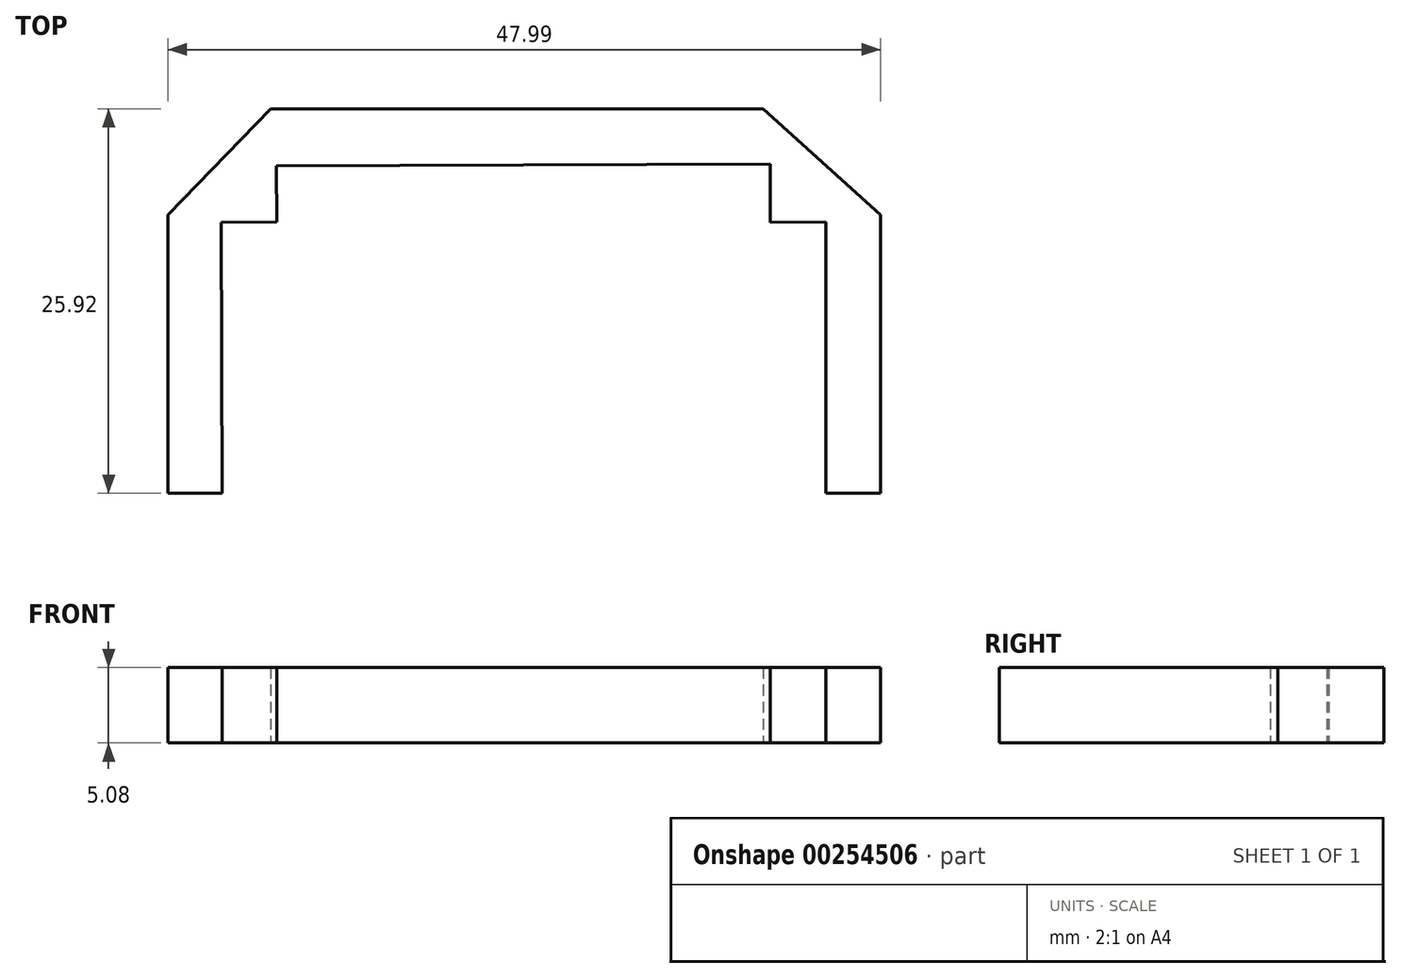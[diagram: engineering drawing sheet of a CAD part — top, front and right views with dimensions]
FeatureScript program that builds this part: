
annotation { "Feature Type Name" : "Feature", "Feature Type Description" : "" }
export const myFeature = defineFeature(function(context is Context, id is Id, definition is map)
    precondition{}
    {
        {
            var Q0;
            Q0=qCreatedBy(makeId("Top.planeOp"),FACE);
            var sketch = newSketch(context, id + "F0", { "sketchPlane" : qUnion([Q0])});
            skLineSegment(sketch, "E0", {"start": v(-33.45, 9.2) * mm, "end": v(-26.8, 16.12) * mm});
            skLineSegment(sketch, "E1", {"start": v(-26.8, 16.12) * mm, "end": v(-22.17, 16.12) * mm});
            skLineSegment(sketch, "E2", {"start": v(-22.17, 16.12) * mm, "end": v(-22.17, 19.99) * mm});
            skLineSegment(sketch, "E3", {"start": v(-22.17, 19.99) * mm, "end": v(-25.8, 19.97) * mm});
            skLineSegment(sketch, "E4", {"start": v(-25.8, 19.97) * mm, "end": v(-25.8, 38.73) * mm});
            skLineSegment(sketch, "E5", {"start": v(-25.8, 38.73) * mm, "end": v(-18.88, 45.9) * mm});
            skLineSegment(sketch, "E6", {"start": v(-18.88, 45.9) * mm, "end": v(14.3, 45.9) * mm});
            skLineSegment(sketch, "E7", {"start": v(14.3, 45.9) * mm, "end": v(22.2, 38.73) * mm});
            skLineSegment(sketch, "E8", {"start": v(22.2, 38.73) * mm, "end": v(22.2, 19.97) * mm});
            skLineSegment(sketch, "E9", {"start": v(22.2, 19.97) * mm, "end": v(18.52, 19.97) * mm});
            skLineSegment(sketch, "E10", {"start": v(18.52, 19.97) * mm, "end": v(18.52, 16.12) * mm});
            skLineSegment(sketch, "E11", {"start": v(18.52, 16.12) * mm, "end": v(22.2, 16.12) * mm});
            skLineSegment(sketch, "E12", {"start": v(22.2, 16.12) * mm, "end": v(29.83, 9.43) * mm});
            skLineSegment(sketch, "E13", {"start": v(29.83, 9.43) * mm, "end": v(29.83, -20.85) * mm});
            skLineSegment(sketch, "E14", {"start": v(29.83, -20.85) * mm, "end": v(22.14, -20.85) * mm});
            skLineSegment(sketch, "E15", {"start": v(22.14, -20.85) * mm, "end": v(22.14, -32.04) * mm});
            skLineSegment(sketch, "E16", {"start": v(22.14, -32.04) * mm, "end": v(19.03, -35.7) * mm});
            skLineSegment(sketch, "E17", {"start": v(19.03, -35.7) * mm, "end": v(3.87, -35.7) * mm});
            skLineSegment(sketch, "E18", {"start": v(3.87, -35.7) * mm, "end": v(3.87, -28.47) * mm});
            skLineSegment(sketch, "E19", {"start": v(3.87, -28.47) * mm, "end": v(-7.29, -28.47) * mm});
            skLineSegment(sketch, "E20", {"start": v(-7.29, -28.47) * mm, "end": v(-7.29, -35.7) * mm});
            skLineSegment(sketch, "E21", {"start": v(-7.29, -35.7) * mm, "end": v(-23.05, -35.7) * mm});
            skLineSegment(sketch, "E22", {"start": v(-23.05, -35.7) * mm, "end": v(-25.8, -32.44) * mm});
            skLineSegment(sketch, "E23", {"start": v(-25.8, -32.44) * mm, "end": v(-25.8, -20.85) * mm});
            skLineSegment(sketch, "E24", {"start": v(-25.8, -20.85) * mm, "end": v(-33.32, -20.85) * mm});
            skLineSegment(sketch, "E25", {"start": v(-33.32, -20.85) * mm, "end": v(-33.45, 9.2) * mm});
            skCircle(sketch, "E26", {"center": v(-11.3, 31.23) * mm, "radius": 5.9 * mm});
            skPoint(sketch, "E26.first.point", {"position": v(-17.19, 30.94) * mm});
            skPoint(sketch, "E26.second.point", {"position": v(-5.4, 31.07) * mm});
            skPoint(sketch, "E26.third.point", {"position": v(-11.26, 25.33) * mm});
            skCircle(sketch, "E27", {"center": v(7.12, 31) * mm, "radius": 5.64 * mm});
            skPoint(sketch, "E27.first.point", {"position": v(1.48, 30.84) * mm});
            skPoint(sketch, "E27.second.point", {"position": v(12.76, 30.78) * mm});
            skPoint(sketch, "E27.third.point", {"position": v(7.1, 36.64) * mm});
            skLineSegment(sketch, "E28.bottom", {"start": v(-14.96, 34.57) * mm, "end": v(-7.5, 34.57) * mm});
            skLineSegment(sketch, "E28.top", {"start": v(-14.96, 27.44) * mm, "end": v(-7.5, 27.44) * mm});
            skLineSegment(sketch, "E28.left", {"start": v(-14.96, 34.57) * mm, "end": v(-14.96, 27.44) * mm});
            skLineSegment(sketch, "E28.right", {"start": v(-7.5, 34.57) * mm, "end": v(-7.5, 27.44) * mm});
            skLineSegment(sketch, "E29.bottom", {"start": v(3.8, 34.28) * mm, "end": v(10.72, 34.28) * mm});
            skLineSegment(sketch, "E29.top", {"start": v(3.8, 27.44) * mm, "end": v(10.72, 27.44) * mm});
            skLineSegment(sketch, "E29.left", {"start": v(3.8, 34.28) * mm, "end": v(3.8, 27.44) * mm});
            skLineSegment(sketch, "E29.right", {"start": v(10.72, 34.28) * mm, "end": v(10.72, 27.44) * mm});
            skLineSegment(sketch, "E30.bottom", {"start": v(7.12, 31) * mm, "end": v(3.8, 31) * mm});
            skLineSegment(sketch, "E30.top", {"start": v(7.12, 34.28) * mm, "end": v(3.8, 34.28) * mm});
            skLineSegment(sketch, "E30.left", {"start": v(7.12, 31) * mm, "end": v(7.12, 34.28) * mm});
            skLineSegment(sketch, "E30.right", {"start": v(3.8, 31) * mm, "end": v(3.8, 34.28) * mm});
            skLineSegment(sketch, "E31.bottom", {"start": v(-11.3, 31.23) * mm, "end": v(-14.96, 31.23) * mm});
            skLineSegment(sketch, "E31.top", {"start": v(-11.3, 34.57) * mm, "end": v(-14.96, 34.57) * mm});
            skLineSegment(sketch, "E31.left", {"start": v(-11.3, 31.23) * mm, "end": v(-11.3, 34.57) * mm});
            skLineSegment(sketch, "E31.right", {"start": v(-14.96, 31.23) * mm, "end": v(-14.96, 34.57) * mm});
            skLineSegment(sketch, "E32.bottom", {"start": v(-3.8, 23.6) * mm, "end": v(0, 23.6) * mm});
            skLineSegment(sketch, "E32.top", {"start": v(-3.8, 19.8) * mm, "end": v(0, 19.8) * mm});
            skLineSegment(sketch, "E32.left", {"start": v(-3.8, 23.6) * mm, "end": v(-3.8, 19.8) * mm});
            skLineSegment(sketch, "E32.right", {"start": v(0, 23.6) * mm, "end": v(0, 19.8) * mm});
            skLineSegment(sketch, "E33.bottom", {"start": v(-7.5, 15.86) * mm, "end": v(3.8, 15.86) * mm});
            skLineSegment(sketch, "E33.top", {"start": v(-7.5, 12.27) * mm, "end": v(3.8, 12.27) * mm});
            skLineSegment(sketch, "E33.left", {"start": v(-7.5, 15.86) * mm, "end": v(-7.5, 12.27) * mm});
            skLineSegment(sketch, "E33.right", {"start": v(3.8, 15.86) * mm, "end": v(3.8, 12.27) * mm});
            skPoint(sketch, "E34.oppositeSnap0", {"position": v(-25.8, -26.64) * mm});
            skLineSegment(sketch, "E34.bottom", {"start": v(-29.45, -9.9) * mm, "end": v(-25.8, -9.9) * mm});
            skLineSegment(sketch, "E34.top", {"start": v(-29.45, -17.27) * mm, "end": v(-25.8, -17.27) * mm});
            skLineSegment(sketch, "E34.left", {"start": v(-29.45, -9.9) * mm, "end": v(-29.45, -17.27) * mm});
            skLineSegment(sketch, "E34.right", {"start": v(-25.8, -9.9) * mm, "end": v(-25.8, -17.27) * mm});
            skLineSegment(sketch, "E35.top", {"start": v(-29.45, 8.74) * mm, "end": v(-25.8, 8.74) * mm});
            skLineSegment(sketch, "E35.left", {"start": v(-29.45, -9.9) * mm, "end": v(-29.45, 8.74) * mm});
            skLineSegment(sketch, "E35.right", {"start": v(-25.8, -9.9) * mm, "end": v(-25.8, 8.74) * mm});
            skLineSegment(sketch, "E36.bottom", {"start": v(22.2, -9.9) * mm, "end": v(25.76, -9.9) * mm});
            skLineSegment(sketch, "E36.top", {"start": v(22.2, -17.27) * mm, "end": v(25.76, -17.27) * mm});
            skLineSegment(sketch, "E36.left", {"start": v(22.2, -9.9) * mm, "end": v(22.2, -17.27) * mm});
            skLineSegment(sketch, "E36.right", {"start": v(25.76, -9.9) * mm, "end": v(25.76, -17.27) * mm});
            skLineSegment(sketch, "E37.top", {"start": v(22.2, 8.7) * mm, "end": v(25.76, 8.7) * mm});
            skLineSegment(sketch, "E37.left", {"start": v(22.2, -9.9) * mm, "end": v(22.2, 8.7) * mm});
            skLineSegment(sketch, "E37.right", {"start": v(25.76, -9.9) * mm, "end": v(25.76, 8.7) * mm});
            skLineSegment(sketch, "E38.bottom", {"start": v(-3.6, -28.47) * mm, "end": v(0, -28.47) * mm});
            skLineSegment(sketch, "E38.top", {"start": v(-3.6, -24.74) * mm, "end": v(0, -24.74) * mm});
            skLineSegment(sketch, "E38.left", {"start": v(-3.6, -28.47) * mm, "end": v(-3.6, -24.74) * mm});
            skLineSegment(sketch, "E38.right", {"start": v(0, -28.47) * mm, "end": v(0, -24.74) * mm});
            skLineSegment(sketch, "E39", {"start": v(-22.24, -24.61) * mm, "end": v(-22.24, -31.85) * mm});
            skLineSegment(sketch, "E40", {"start": v(-22.24, -31.85) * mm, "end": v(-11.06, -31.85) * mm});
            skLineSegment(sketch, "E41", {"start": v(-11.06, -31.85) * mm, "end": v(-11.06, -28.48) * mm});
            skLineSegment(sketch, "E42", {"start": v(-11.06, -28.48) * mm, "end": v(-7.29, -28.47) * mm});
            skLineSegment(sketch, "E43", {"start": v(-7.29, -24.61) * mm, "end": v(-22.24, -24.61) * mm});
            skLineSegment(sketch, "E44", {"start": v(-7.29, -24.61) * mm, "end": v(-7.29, -28.47) * mm});
            skLineSegment(sketch, "E45", {"start": v(3.87, -28.47) * mm, "end": v(3.87, -24.61) * mm});
            skLineSegment(sketch, "E46", {"start": v(3.87, -24.61) * mm, "end": v(18.56, -24.61) * mm});
            skLineSegment(sketch, "E47", {"start": v(18.56, -24.61) * mm, "end": v(18.56, -31.97) * mm});
            skLineSegment(sketch, "E48", {"start": v(18.56, -31.97) * mm, "end": v(7.4, -31.97) * mm});
            skLineSegment(sketch, "E49", {"start": v(7.4, -31.97) * mm, "end": v(7.4, -28.47) * mm});
            skLineSegment(sketch, "E50", {"start": v(7.4, -28.47) * mm, "end": v(3.87, -28.47) * mm});
            skLineSegment(sketch, "E51", {"start": v(-22.17, 19.99) * mm, "end": v(-22.24, 38.23) * mm});
            skLineSegment(sketch, "E52", {"start": v(-22.24, 38.23) * mm, "end": v(-18.48, 38.25) * mm});
            skLineSegment(sketch, "E53", {"start": v(-18.48, 38.25) * mm, "end": v(-18.5, 42.04) * mm});
            skLineSegment(sketch, "E54", {"start": v(-18.5, 42.04) * mm, "end": v(14.76, 42.16) * mm});
            skLineSegment(sketch, "E55", {"start": v(14.76, 42.16) * mm, "end": v(14.78, 38.23) * mm});
            skLineSegment(sketch, "E56", {"start": v(14.78, 38.23) * mm, "end": v(18.52, 38.24) * mm});
            skLineSegment(sketch, "E57", {"start": v(18.52, 38.24) * mm, "end": v(18.52, 19.97) * mm});
            skLineSegment(sketch, "E58", {"start": v(3.8, 15.86) * mm, "end": v(3.8, 19.97) * mm});
            skLineSegment(sketch, "E59", {"start": v(3.8, 19.97) * mm, "end": v(18.52, 19.97) * mm});
            skLineSegment(sketch, "E60", {"start": v(-7.5, 15.86) * mm, "end": v(-7.5, 19.99) * mm});
            skLineSegment(sketch, "E61", {"start": v(-7.5, 19.99) * mm, "end": v(-22.17, 19.99) * mm});
            skLineSegment(sketch, "E62", {"start": v(-22.23, 12.38) * mm, "end": v(-22.23, -21.38) * mm});
            skLineSegment(sketch, "E63", {"start": v(-22.23, -21.38) * mm, "end": v(18.48, -21.38) * mm});
            skLineSegment(sketch, "E64", {"start": v(18.48, -21.38) * mm, "end": v(18.48, 12.34) * mm});
            skLineSegment(sketch, "E65", {"start": v(18.48, 12.34) * mm, "end": v(14.65, 12.34) * mm});
            skLineSegment(sketch, "E66", {"start": v(14.65, 12.34) * mm, "end": v(14.65, 15.86) * mm});
            skLineSegment(sketch, "E67", {"start": v(14.65, 15.86) * mm, "end": v(3.8, 15.86) * mm});
            skLineSegment(sketch, "E68", {"start": v(-22.23, 12.38) * mm, "end": v(-18.53, 12.38) * mm});
            skLineSegment(sketch, "E69", {"start": v(-18.53, 12.38) * mm, "end": v(-18.53, 15.86) * mm});
            skLineSegment(sketch, "E70", {"start": v(-18.53, 15.86) * mm, "end": v(-7.5, 15.86) * mm});
            skLineSegment(sketch, "E71.bottom", {"start": v(-7.42, -28.31) * mm, "end": v(-7.13, -28.31) * mm});
            skLineSegment(sketch, "E71.top", {"start": v(-7.42, -28.63) * mm, "end": v(-7.13, -28.63) * mm});
            skLineSegment(sketch, "E71.left", {"start": v(-7.42, -28.31) * mm, "end": v(-7.42, -28.63) * mm});
            skLineSegment(sketch, "E71.right", {"start": v(-7.13, -28.31) * mm, "end": v(-7.13, -28.63) * mm});
            skLineSegment(sketch, "E72.bottom", {"start": v(3.95, -28.38) * mm, "end": v(3.78, -28.38) * mm});
            skLineSegment(sketch, "E72.top", {"start": v(3.95, -28.56) * mm, "end": v(3.78, -28.56) * mm});
            skLineSegment(sketch, "E72.left", {"start": v(3.95, -28.38) * mm, "end": v(3.95, -28.56) * mm});
            skLineSegment(sketch, "E72.right", {"start": v(3.78, -28.38) * mm, "end": v(3.78, -28.56) * mm});
            skSolve(sketch);
        }
        {
            var Q0;
            Q0=makeQuery(id+"F0.imprint","IMPRINT",FACE,{"disambiguationData":[TD([[makeQuery(id+"F0.imprint","IMPRINT",EDGE,{"derivedFrom":sQuery(id+"F0.wireOp",EDGE,"E3")}),-1.0]])]});
            extrude(context, id + "F1", {"entities" : qUnion([Q0]), "depth" : 5.08 * mm});
        }
    });
